# Revit family: PROOX Bag- and clothes holder EN
name_source: partatom
category: Furniture
revit_build: Autodesk Revit 2014 (Build: 20130308_1515(x64)
units: mm (PartAtom-declared; Revit-internal decimal feet)

## types (2) — shared parameters
BIM objects producer = www.BIMtelligent.eu
Manufacturer = PROOX Ltd.
Product data sheet = http://www.proox.com
URL = http://www.proox.com

## per-type parameters (varying)
| type | Cost | Description | EAN-No. | Material | Model | Specifications |
| ONE pure | 23 $ | bag- and clothes hook PROOX ONE pure made from stainless steel | 9120050350724 | PROOX Stainless steel, satin finish | PU-568 | Bag- and clothes hook made from stainless steel. For wall mounting. Surface with fine brushed structure. The screw has a male threaded portion that mates with a threaded hole in the rear of the hook for a concealed mounting system. Can be glued with Loctite for secure fixing, if required. |
| ONE dark passion | 25 $ | bag- and clothes hook PROOX ONE dark passion made from aluminum black anodized | 9120050350984 | PROOX Aluminum, black anodised | DP-568 | Bag- and clothes hook made out from glass pearl blasted and black anodised aluminum. Intended for wall mounting. The screw has a male threaded portion that mates with a threaded hole in the rear of the hook for a concealed mounting system. Can be glued with Loctite for secure fixing, if required. |

note: column(s) folded — value = type name in every type: Type Comments

## geometry (parser evidence)
native form markers: Sweep x1
no freeform markers — native parametric forms only
